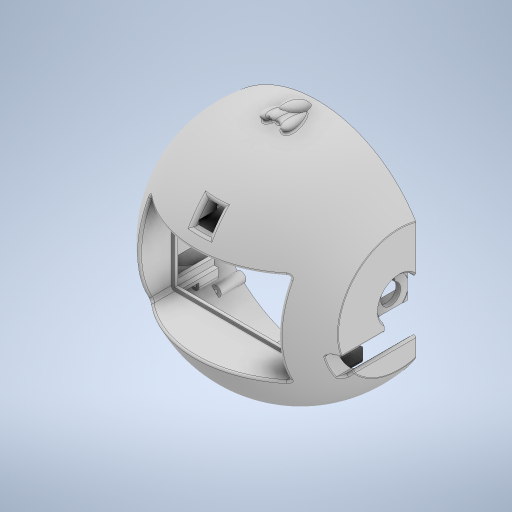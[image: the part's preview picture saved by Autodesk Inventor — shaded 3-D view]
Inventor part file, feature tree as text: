
AUTODESK INVENTOR PART (.ipt)
format: ipt  version: 2023 (Build 270158000, 158)  size: 1,363,968 bytes
history: native  units: mm
features: extrude x38, sketch x34, fillet x14, projected_geometry x9, other x4, chamfer x4, revolve x3, shell x1, pattern_circular x1, mirror x1
ambient origin geometry x8: Origin, YZ Plane, XZ Plane, XY Plane, X Axis, Y Axis, Z Axis, Center Point
bodies: Body1 (feature_tree)
feature tree (109):
  other  "솔리드1"
  sketch  "스케치1"
  revolve  "회전1"
  other  "작업 평면1"
  extrude  "돌출2"  Depth=85.0mm
  other  "작업 평면2"
  extrude  "돌출3"  Depth=56.0mm
  shell  "쉘1"  Thickness=17.0mm
  extrude  "돌출4"  Depth=140.0mm
  extrude  "돌출5"  Depth=4.0mm
  extrude  "돌출6"  TaperAngle=360.0deg  [1 undecoded]
  extrude  "돌출7"  Depth=84.0mm
  extrude  "돌출8"  Depth=55.0mm
  extrude  "돌출9"  Depth=32.0mm TaperAngle=0.0deg
  extrude  "돌출10"  [1 undecoded]
  extrude  "돌출11"  Depth=165.25mm TaperAngle=0.0deg
  extrude  "돌출12"  Depth=4.0mm
  fillet  "모깎기1"  Radius=85.5mm
  extrude  "돌출13"  Depth=57.0mm
  sketch  "스케치16"
  extrude  "돌출14"  Depth=25.5mm TaperAngle=0.0deg
  extrude  "돌출16"  Depth=17.0mm TaperAngle=0.0deg
  fillet  "모깎기2"  Radius=16.5mm
  fillet  "모깎기3"  Radius=10.0mm
  fillet  "모깎기4"  Radius=18.5mm
  fillet  "모깎기5"  Radius=13.0mm
  extrude  "돌출17"  Depth=12.0mm
  sketch  "스케치19"
  extrude  "돌출19"  Depth=35.25mm TaperAngle=0.0deg
  extrude  "돌출20"  Depth=2.0mm
  extrude  "돌출21"  Depth=16.0mm TaperAngle=0.0deg
  sketch  "스케치22"
  extrude  "돌출22"  Depth=2.0mm
  extrude  "돌출24"  Depth=27.0mm
  extrude  "돌출26"  Depth=9.0mm
  extrude  "돌출27"  Depth=10.0mm TaperAngle=0.0deg
  extrude  "돌출28"  Depth=8.0mm
  fillet  "모깎기6"  Radius=23.0mm
  chamfer  "모따기3"  Distance=20.0mm
  extrude  "돌출29"  Depth=10.0mm TaperAngle=0.0deg
  extrude  "돌출30"  Depth=7.5mm
  extrude  "돌출31"  Depth=50.0mm
  extrude  "돌출32"  Depth=20.0mm TaperAngle=0.0deg
  fillet  "모깎기7"  Radius=2.0mm
  chamfer  "모따기6"  Distance=5.0mm
  chamfer  "모따기7"  Distance=5.0mm
  chamfer  "모따기8"  Distance=2.5mm
  fillet  "모깎기9"  Radius=12.0mm
  other  "작업 평면3"
  extrude  "돌출33"  Depth=0.5mm
  extrude  "돌출34"  Depth=1.0mm
  fillet  "모깎기14"  Radius=11.0mm
  extrude  "돌출42"  Depth=25.3mm
  extrude  "돌출43"  Depth=25.5mm TaperAngle=0.0deg
  extrude  "돌출44"  Depth=0.5mm
  fillet  "모깎기16"  Radius=2.0mm
  sketch  "스케치43"
  extrude  "돌출45"  Depth=15.0mm TaperAngle=0.0deg
  extrude  "돌출46"  Depth=80.0mm TaperAngle=360.0deg
  extrude  "돌출47"  Depth=12.5mm
  extrude  "돌출48"  Depth=23.1mm
  fillet  "모깎기17"  Radius=4.0mm
  fillet  "모깎기18"  Radius=4.55mm
  extrude  "돌출49"  Depth=12.0mm
  extrude  "돌출50"  Depth=12.0mm
  sketch  "스케치46"
  revolve  "회전2"
  pattern_circular  "원형 패턴1"  [2 undecoded]
  mirror  "미러1"
  fillet  "모깎기19"  Radius=288.5mm
  fillet  "모깎기20"  Radius=2.0mm
  revolve  "회전3"
  sketch  "스케치2"
  sketch  "스케치3"
  sketch  "스케치5"
  projected_geometry  "투영된 루프1"
  sketch  "스케치6"
  projected_geometry  "투영된 루프2"
  sketch  "스케치7"
  sketch  "스케치8"
  sketch  "스케치9"
  sketch  "스케치10"
  sketch  "스케치11"
  projected_geometry  "투영된 루프3"
  sketch  "스케치12"
  sketch  "스케치13"
  sketch  "스케치15"
  projected_geometry  "투영된 루프4"
  sketch  "스케치17"
  sketch  "스케치18"
  sketch  "스케치20"
  sketch  "스케치21"
  projected_geometry  "투영된 루프5"
  sketch  "스케치23"
  sketch  "스케치24"
  sketch  "스케치25"
  sketch  "스케치26"
  sketch  "스케치27"
  sketch  "스케치29"
  sketch  "스케치30"
  projected_geometry  "투영된 루프6"
  sketch  "스케치32"
  projected_geometry  "투영된 루프7"
  sketch  "스케치41"
  sketch  "스케치42"
  sketch  "스케치44"
  projected_geometry  "투영된 루프14"
  sketch  "스케치45"
  projected_geometry  "투영된 루프15"
note: 4 required parameter values undecoded (feature->parameter linkage not recoverable at this tier; creation-order binding heuristic only, values carry confidence <= 0.55)
